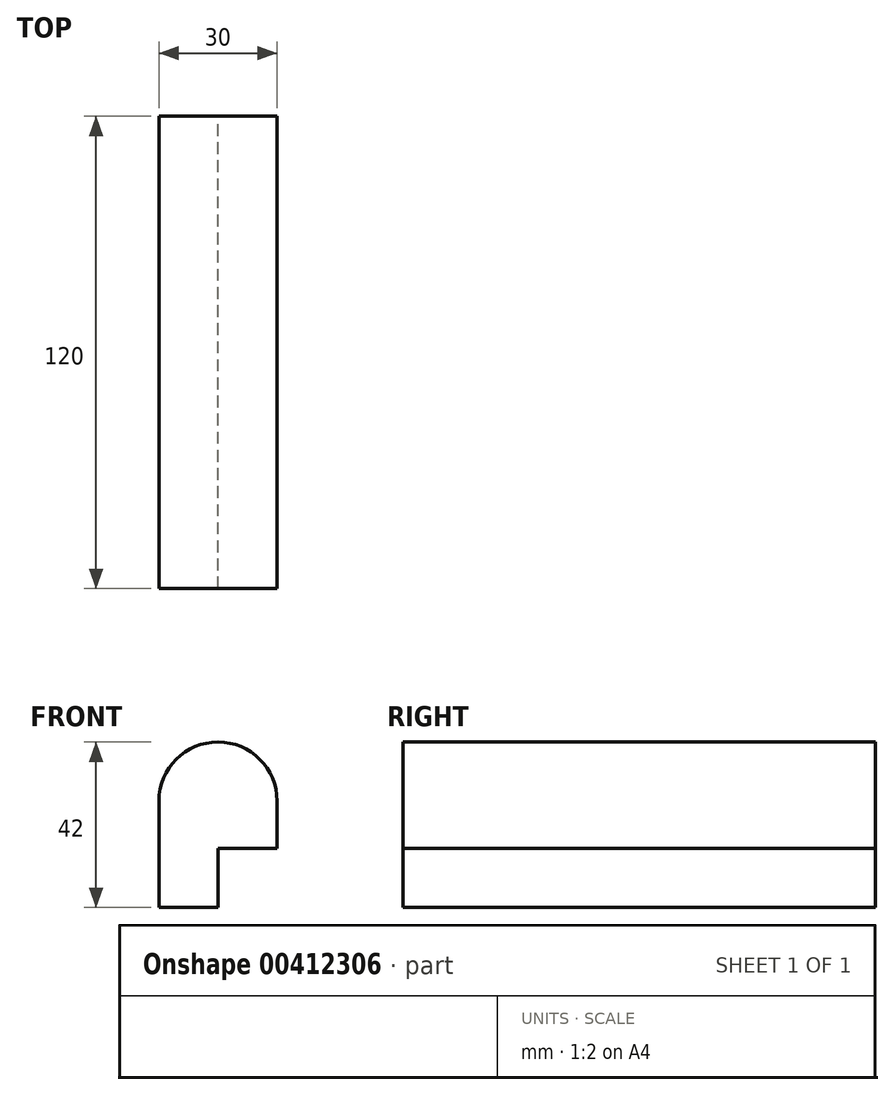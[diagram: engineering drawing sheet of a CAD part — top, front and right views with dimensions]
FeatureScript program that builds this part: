
annotation { "Feature Type Name" : "Feature", "Feature Type Description" : "" }
export const myFeature = defineFeature(function(context is Context, id is Id, definition is map)
    precondition{}
    {
        {
            var Q0;
            Q0=qCreatedBy(makeId("Front.planeOp"),FACE);
            var sketch = newSketch(context, id + "F0", { "sketchPlane" : qUnion([Q0])});
            skLineSegment(sketch, "E0", {"start": v(0, 0) * mm, "end": v(0, 15) * mm});
            skLineSegment(sketch, "E1", {"start": v(0, 15) * mm, "end": v(15, 15) * mm});
            skLineSegment(sketch, "E2", {"start": v(15, 15) * mm, "end": v(15, 27) * mm});
            skLineSegment(sketch, "E3", {"start": v(15, 27) * mm, "end": v(-15, 27) * mm});
            skLineSegment(sketch, "E4", {"start": v(-15, 27) * mm, "end": v(-15, 0) * mm});
            skLineSegment(sketch, "E5", {"start": v(-15, 0) * mm, "end": v(0, 0) * mm});
            skArc(sketch, "E6", {"start": v(15, 27) * mm, "mid": v(0, 42) * mm, "end": v(-15, 27) * mm});
            skSolve(sketch);
        }
        {
            var Q0;
            Q0 = qSketchRegion(id + "F0", true);
            extrude(context, id + "F1", {"entities" : qUnion([Q0]), "depth" : 120 * mm});
        }
    });
